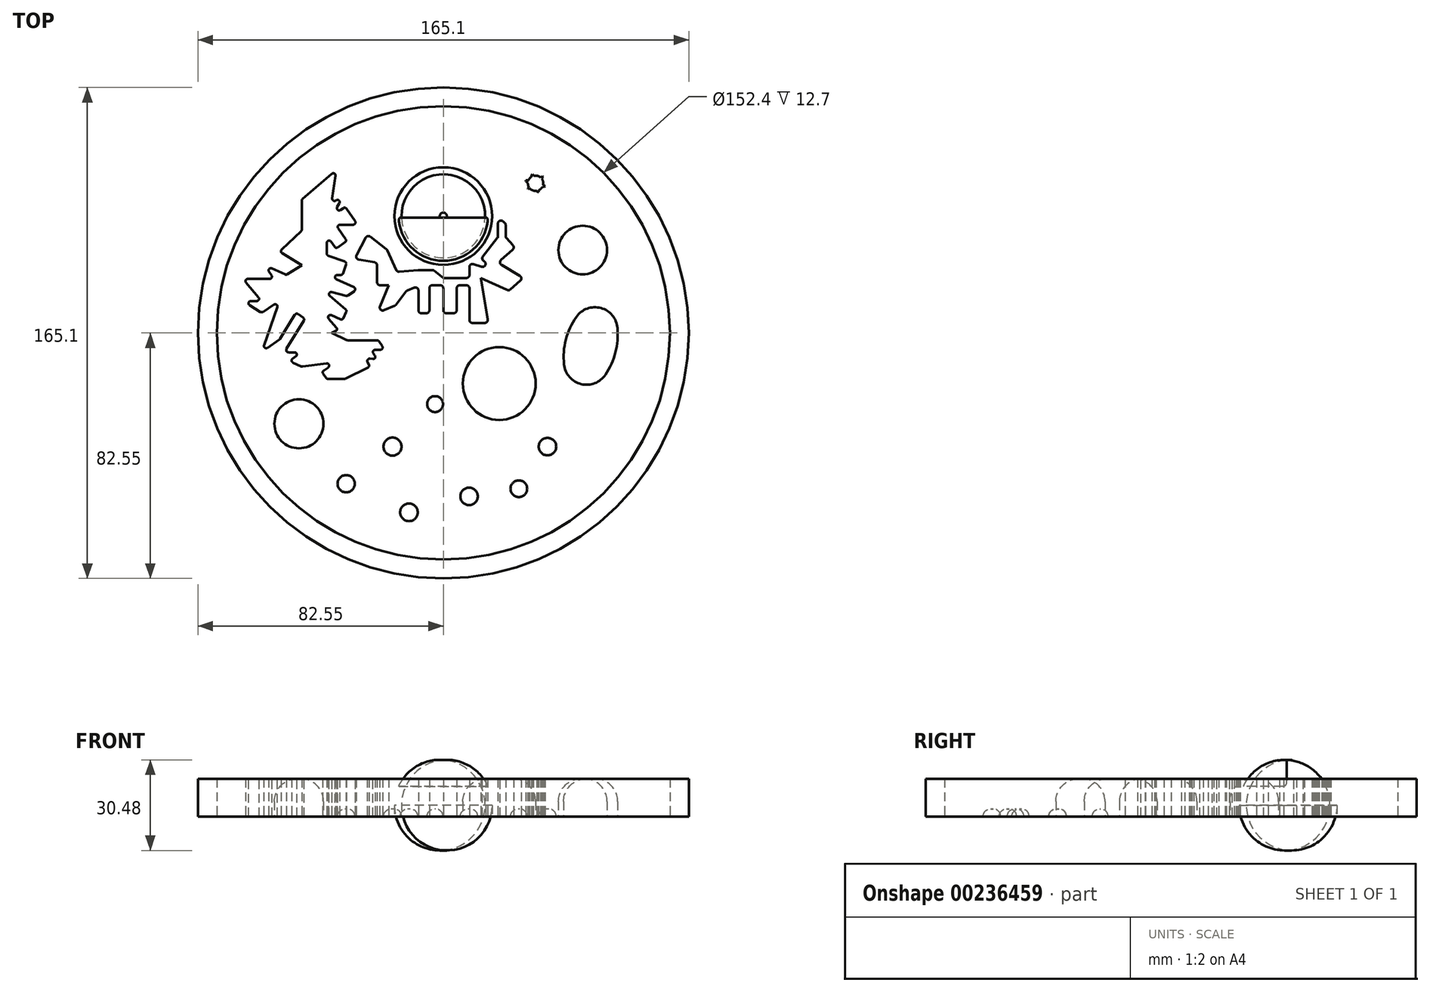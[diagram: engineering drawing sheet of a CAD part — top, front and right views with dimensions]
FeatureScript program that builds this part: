
annotation { "Feature Type Name" : "Feature", "Feature Type Description" : "" }
export const myFeature = defineFeature(function(context is Context, id is Id, definition is map)
    precondition{}
    {
        {
            var Q0;
            Q0=qCreatedBy(makeId("Top.planeOp"),FACE);
            var sketch = newSketch(context, id + "F0", { "sketchPlane" : qUnion([Q0])});
            skCircle(sketch, "E0", {"center": v(0, 0) * mm, "radius": 76.2 * mm});
            skCircle(sketch, "E1", {"center": v(0, 0) * mm, "radius": 82.55 * mm});
            skLineSegment(sketch, "E2", {"start": v(76.2, 0) * mm, "end": v(82.55, 0) * mm});
            skLineSegment(sketch, "E3", {"start": v(-76.2, 0) * mm, "end": v(-82.55, 0) * mm});
            skSolve(sketch);
        }
        {
            var Q0;
            {var subQ0=sQuery(id+"F0.wireOp",EDGE,"E2");Q0=makeQuery(id+"F0.imprint","IMPRINT",FACE,{"disambiguationData":[TD([[makeQuery(id+"F0.imprint","IMPRINT",EDGE,{"derivedFrom":subQ0}),1.0]])]});}
            var Q1;
            {var subQ0=sQuery(id+"F0.wireOp",EDGE,"E2");Q1=makeQuery(id+"F0.imprint","IMPRINT",FACE,{"disambiguationData":[TD([[makeQuery(id+"F0.imprint","IMPRINT",EDGE,{"derivedFrom":subQ0}),-1.0]])]});}
            extrude(context, id + "F1", {"entities" : qUnion([Q0, Q1]), "depth" : 12.7 * mm});
        }
        {
            var Q0;
            Q0=qCreatedBy(makeId("Top.planeOp"),FACE);
            var sketch = newSketch(context, id + "F2", { "sketchPlane" : qUnion([Q0])});
            skCircle(sketch, "E4", {"center": v(0, 39.3) * mm, "radius": 16.42 * mm});
            skSolve(sketch);
        }
        {
            var Q0;
            Q0=makeQuery(id+"F2.imprint","IMPRINT",FACE,{"disambiguationData":[TD([[makeQuery(id+"F2.imprint","IMPRINT",EDGE,{"derivedFrom":sQuery(id+"F2.wireOp",EDGE,"E4")}),1.0]])]});
            extrude(context, id + "F3", {"entities" : qUnion([Q0]), "depth" : 19.05 * mm});
        }
        {
            var Q0;
            Q0=makeQuery(id+"F3.opExtrude","CAP_EDGE",EDGE,{"disambiguationData":[OSD([sQuery(id+"F2.wireOp",EDGE,"E4")])],"isStart":false});
            fillet(context, id + "F4", {"entities" : qUnion([Q0]), "radius" : 15.24 * mm, "tangentPropagation" : true, "allowEdgeOverflow" : false});
        }
        {
            var Q0;
            Q0=qCreatedBy(makeId("Top.planeOp"),FACE);
            var sketch = newSketch(context, id + "F5", { "sketchPlane" : qUnion([Q0])});
            skLineSegment(sketch, "E5", {"start": v(-8.37, 15.82) * mm, "end": v(-8.37, 6.64) * mm});
            skLineSegment(sketch, "E6", {"start": v(-8.37, 6.64) * mm, "end": v(-4.7, 6.64) * mm});
            skLineSegment(sketch, "E7", {"start": v(-4.7, 6.64) * mm, "end": v(-4.7, 16.03) * mm});
            skLineSegment(sketch, "E8", {"start": v(-4.7, 16.03) * mm, "end": v(0, 16.03) * mm});
            skLineSegment(sketch, "E9", {"start": v(0, 16.03) * mm, "end": v(0, 6.64) * mm});
            skLineSegment(sketch, "E10", {"start": v(0, 6.64) * mm, "end": v(4.5, 6.64) * mm});
            skLineSegment(sketch, "E11", {"start": v(4.5, 6.64) * mm, "end": v(4.5, 16.03) * mm});
            skLineSegment(sketch, "E12", {"start": v(4.5, 16.03) * mm, "end": v(8.78, 16.03) * mm});
            skLineSegment(sketch, "E13", {"start": v(8.78, 16.03) * mm, "end": v(8.78, 3.37) * mm});
            skLineSegment(sketch, "E14", {"start": v(8.78, 3.37) * mm, "end": v(15.1, 3.37) * mm});
            skLineSegment(sketch, "E15", {"start": v(15.1, 3.37) * mm, "end": v(12.66, 18.48) * mm});
            skLineSegment(sketch, "E16", {"start": v(12.66, 18.48) * mm, "end": v(22.05, 14.2) * mm});
            skLineSegment(sketch, "E17", {"start": v(22.05, 14.2) * mm, "end": v(26.95, 18.48) * mm});
            skLineSegment(sketch, "E18", {"start": v(26.95, 18.48) * mm, "end": v(18.38, 23.58) * mm});
            skLineSegment(sketch, "E19", {"start": v(18.38, 23.58) * mm, "end": v(24.1, 28.69) * mm});
            skLineSegment(sketch, "E20", {"start": v(24.1, 28.69) * mm, "end": v(20.95, 32.2) * mm});
            skLineSegment(sketch, "E21", {"start": v(20.95, 32.2) * mm, "end": v(20.95, 36.86) * mm});
            skLineSegment(sketch, "E22", {"start": v(20.95, 36.86) * mm, "end": v(18.38, 38.9) * mm});
            skLineSegment(sketch, "E23", {"start": v(18.38, 38.9) * mm, "end": v(18.38, 32.16) * mm});
            skLineSegment(sketch, "E24", {"start": v(18.38, 32.16) * mm, "end": v(15.1, 28.04) * mm});
            skLineSegment(sketch, "E25", {"start": v(15.1, 28.04) * mm, "end": v(12.66, 24.95) * mm});
            skLineSegment(sketch, "E26", {"start": v(18.38, 20.52) * mm, "end": v(12.66, 24.95) * mm});
            skLineSegment(sketch, "E27", {"start": v(18.38, 20.52) * mm, "end": v(8.78, 23.58) * mm});
            skLineSegment(sketch, "E28", {"start": v(8.78, 23.58) * mm, "end": v(8.78, 18.48) * mm});
            skLineSegment(sketch, "E29", {"start": v(8.78, 18.48) * mm, "end": v(0, 18.48) * mm});
            skLineSegment(sketch, "E30", {"start": v(0, 18.48) * mm, "end": v(-3.4, 21.17) * mm});
            skLineSegment(sketch, "E31", {"start": v(-3.4, 21.17) * mm, "end": v(-8.37, 21.17) * mm});
            skLineSegment(sketch, "E32", {"start": v(-8.37, 21.17) * mm, "end": v(-15.52, 20.52) * mm});
            skLineSegment(sketch, "E33", {"start": v(-15.52, 20.52) * mm, "end": v(-18.99, 28.08) * mm});
            skLineSegment(sketch, "E34", {"start": v(-18.99, 28.08) * mm, "end": v(-25.52, 33.13) * mm});
            skLineSegment(sketch, "E35", {"start": v(-25.52, 33.13) * mm, "end": v(-29.81, 24.95) * mm});
            skLineSegment(sketch, "E36", {"start": v(-29.81, 24.95) * mm, "end": v(-22.26, 23.58) * mm});
            skLineSegment(sketch, "E37", {"start": v(-22.26, 23.58) * mm, "end": v(-22.26, 16.03) * mm});
            skLineSegment(sketch, "E38", {"start": v(-22.26, 16.03) * mm, "end": v(-18.38, 16.03) * mm});
            skLineSegment(sketch, "E39", {"start": v(-18.38, 16.03) * mm, "end": v(-22.26, 6.64) * mm});
            skLineSegment(sketch, "E40", {"start": v(-22.26, 6.64) * mm, "end": v(-16.13, 9.3) * mm});
            skLineSegment(sketch, "E41", {"start": v(-16.13, 9.3) * mm, "end": v(-12.34, 14.2) * mm});
            skLineSegment(sketch, "E42", {"start": v(-12.34, 14.2) * mm, "end": v(-8.37, 15.82) * mm});
            skSolve(sketch);
        }
        {
            var Q0;
            Q0 = qSketchRegion(id + "F5", true);
            extrude(context, id + "F6", {"entities" : qUnion([Q0]), "depth" : 12.7 * mm});
        }
        {
            var Q0;
            Q0=makeQuery(id+"F6.opExtrude","SWEPT_EDGE",EDGE,{"disambiguationData":[OSD([sQuery(id+"F5.wireOp",EDGE,"E39"),sQuery(id+"F5.wireOp",EDGE,"E40")])]});
            var Q1;
            Q1=makeQuery(id+"F6.opExtrude","SWEPT_EDGE",EDGE,{"disambiguationData":[OSD([sQuery(id+"F5.wireOp",EDGE,"E40"),sQuery(id+"F5.wireOp",EDGE,"E41")])]});
            var Q2;
            Q2=makeQuery(id+"F6.opExtrude","SWEPT_EDGE",EDGE,{"disambiguationData":[OSD([sQuery(id+"F5.wireOp",EDGE,"E41"),sQuery(id+"F5.wireOp",EDGE,"E42")])]});
            var Q3;
            Q3=makeQuery(id+"F6.opExtrude","SWEPT_EDGE",EDGE,{"disambiguationData":[OSD([sQuery(id+"F5.wireOp",EDGE,"E5"),sQuery(id+"F5.wireOp",EDGE,"E42")])]});
            var Q4;
            Q4=makeQuery(id+"F6.opExtrude","SWEPT_EDGE",EDGE,{"disambiguationData":[OSD([sQuery(id+"F5.wireOp",EDGE,"E37"),sQuery(id+"F5.wireOp",EDGE,"E38")])]});
            var Q5;
            Q5=makeQuery(id+"F6.opExtrude","SWEPT_EDGE",EDGE,{"disambiguationData":[OSD([sQuery(id+"F5.wireOp",EDGE,"E36"),sQuery(id+"F5.wireOp",EDGE,"E37")])]});
            var Q6;
            Q6=makeQuery(id+"F6.opExtrude","SWEPT_EDGE",EDGE,{"disambiguationData":[OSD([sQuery(id+"F5.wireOp",EDGE,"E35"),sQuery(id+"F5.wireOp",EDGE,"E36")])]});
            var Q7;
            Q7=makeQuery(id+"F6.opExtrude","SWEPT_EDGE",EDGE,{"disambiguationData":[OSD([sQuery(id+"F5.wireOp",EDGE,"E8"),sQuery(id+"F5.wireOp",EDGE,"E9")])]});
            var Q8;
            Q8=makeQuery(id+"F6.opExtrude","SWEPT_EDGE",EDGE,{"disambiguationData":[OSD([sQuery(id+"F5.wireOp",EDGE,"E7"),sQuery(id+"F5.wireOp",EDGE,"E8")])]});
            var Q9;
            Q9=makeQuery(id+"F6.opExtrude","SWEPT_EDGE",EDGE,{"disambiguationData":[OSD([sQuery(id+"F5.wireOp",EDGE,"E6"),sQuery(id+"F5.wireOp",EDGE,"E7")])]});
            var Q10;
            Q10=makeQuery(id+"F6.opExtrude","SWEPT_EDGE",EDGE,{"disambiguationData":[OSD([sQuery(id+"F5.wireOp",EDGE,"E5"),sQuery(id+"F5.wireOp",EDGE,"E6")])]});
            var Q11;
            Q11=makeQuery(id+"F6.opExtrude","SWEPT_EDGE",EDGE,{"disambiguationData":[OSD([sQuery(id+"F5.wireOp",EDGE,"E9"),sQuery(id+"F5.wireOp",EDGE,"E10")])]});
            var Q12;
            Q12=makeQuery(id+"F6.opExtrude","SWEPT_EDGE",EDGE,{"disambiguationData":[OSD([sQuery(id+"F5.wireOp",EDGE,"E10"),sQuery(id+"F5.wireOp",EDGE,"E11")])]});
            var Q13;
            Q13=makeQuery(id+"F6.opExtrude","SWEPT_EDGE",EDGE,{"disambiguationData":[OSD([sQuery(id+"F5.wireOp",EDGE,"E11"),sQuery(id+"F5.wireOp",EDGE,"E12")])]});
            var Q14;
            Q14=makeQuery(id+"F6.opExtrude","SWEPT_EDGE",EDGE,{"disambiguationData":[OSD([sQuery(id+"F5.wireOp",EDGE,"E12"),sQuery(id+"F5.wireOp",EDGE,"E13")])]});
            var Q15;
            Q15=makeQuery(id+"F6.opExtrude","SWEPT_EDGE",EDGE,{"disambiguationData":[OSD([sQuery(id+"F5.wireOp",EDGE,"E13"),sQuery(id+"F5.wireOp",EDGE,"E14")])]});
            var Q16;
            Q16=makeQuery(id+"F6.opExtrude","SWEPT_EDGE",EDGE,{"disambiguationData":[OSD([sQuery(id+"F5.wireOp",EDGE,"E14"),sQuery(id+"F5.wireOp",EDGE,"E15")])]});
            var Q17;
            Q17=makeQuery(id+"F6.opExtrude","SWEPT_EDGE",EDGE,{"disambiguationData":[OSD([sQuery(id+"F5.wireOp",EDGE,"E16"),sQuery(id+"F5.wireOp",EDGE,"E17")])]});
            var Q18;
            Q18=makeQuery(id+"F6.opExtrude","SWEPT_EDGE",EDGE,{"disambiguationData":[OSD([sQuery(id+"F5.wireOp",EDGE,"E17"),sQuery(id+"F5.wireOp",EDGE,"E18")])]});
            var Q19;
            Q19=makeQuery(id+"F6.opExtrude","SWEPT_EDGE",EDGE,{"disambiguationData":[OSD([sQuery(id+"F5.wireOp",EDGE,"E18"),sQuery(id+"F5.wireOp",EDGE,"E19")])]});
            var Q20;
            Q20=makeQuery(id+"F6.opExtrude","SWEPT_EDGE",EDGE,{"disambiguationData":[OSD([sQuery(id+"F5.wireOp",EDGE,"E19"),sQuery(id+"F5.wireOp",EDGE,"E20")])]});
            var Q21;
            Q21=makeQuery(id+"F6.opExtrude","SWEPT_EDGE",EDGE,{"disambiguationData":[OSD([sQuery(id+"F5.wireOp",EDGE,"E20"),sQuery(id+"F5.wireOp",EDGE,"E21")])]});
            var Q22;
            Q22=makeQuery(id+"F6.opExtrude","SWEPT_EDGE",EDGE,{"disambiguationData":[OSD([sQuery(id+"F5.wireOp",EDGE,"E21"),sQuery(id+"F5.wireOp",EDGE,"E22")])]});
            var Q23;
            Q23=makeQuery(id+"F6.opExtrude","SWEPT_EDGE",EDGE,{"disambiguationData":[OSD([sQuery(id+"F5.wireOp",EDGE,"E22"),sQuery(id+"F5.wireOp",EDGE,"E23")])]});
            var Q24;
            Q24=makeQuery(id+"F6.opExtrude","SWEPT_EDGE",EDGE,{"disambiguationData":[OSD([sQuery(id+"F5.wireOp",EDGE,"E23"),sQuery(id+"F5.wireOp",EDGE,"E24")])]});
            var Q25;
            Q25=makeQuery(id+"F6.opExtrude","SWEPT_EDGE",EDGE,{"disambiguationData":[OSD([sQuery(id+"F5.wireOp",EDGE,"E25"),sQuery(id+"F5.wireOp",EDGE,"E26")])]});
            var Q26;
            Q26=makeQuery(id+"F6.opExtrude","SWEPT_EDGE",EDGE,{"disambiguationData":[OSD([sQuery(id+"F5.wireOp",EDGE,"E26"),sQuery(id+"F5.wireOp",EDGE,"E27")])]});
            var Q27;
            Q27=makeQuery(id+"F6.opExtrude","SWEPT_EDGE",EDGE,{"disambiguationData":[OSD([sQuery(id+"F5.wireOp",EDGE,"E28"),sQuery(id+"F5.wireOp",EDGE,"E29")])]});
            var Q28;
            Q28=makeQuery(id+"F6.opExtrude","SWEPT_EDGE",EDGE,{"disambiguationData":[OSD([sQuery(id+"F5.wireOp",EDGE,"E27"),sQuery(id+"F5.wireOp",EDGE,"E28")])]});
            var Q29;
            Q29=makeQuery(id+"F6.opExtrude","SWEPT_EDGE",EDGE,{"disambiguationData":[OSD([sQuery(id+"F5.wireOp",EDGE,"E31"),sQuery(id+"F5.wireOp",EDGE,"E32")])]});
            var Q30;
            Q30=makeQuery(id+"F6.opExtrude","SWEPT_EDGE",EDGE,{"disambiguationData":[OSD([sQuery(id+"F5.wireOp",EDGE,"E30"),sQuery(id+"F5.wireOp",EDGE,"E31")])]});
            var Q31;
            Q31=makeQuery(id+"F6.opExtrude","SWEPT_EDGE",EDGE,{"disambiguationData":[OSD([sQuery(id+"F5.wireOp",EDGE,"E33"),sQuery(id+"F5.wireOp",EDGE,"E34")])]});
            var Q32;
            Q32=makeQuery(id+"F6.opExtrude","SWEPT_EDGE",EDGE,{"disambiguationData":[OSD([sQuery(id+"F5.wireOp",EDGE,"E32"),sQuery(id+"F5.wireOp",EDGE,"E33")])]});
            var Q33;
            Q33=makeQuery(id+"F6.opExtrude","SWEPT_EDGE",EDGE,{"disambiguationData":[OSD([sQuery(id+"F5.wireOp",EDGE,"E34"),sQuery(id+"F5.wireOp",EDGE,"E35")])]});
            fillet(context, id + "F7", {"entities" : qUnion([Q0, Q1, Q2, Q3, Q4, Q5, Q6, Q7, Q8, Q9, Q10, Q11, Q12, Q13, Q14, Q15, Q16, Q17, Q18, Q19, Q20, Q21, Q22, Q23, Q24, Q25, Q26, Q27, Q28, Q29, Q30, Q31, Q32, Q33]), "radius" : 1.02 * mm, "tangentPropagation" : true, "allowEdgeOverflow" : false});
        }
        {
            var Q0;
            Q0=makeQuery(id+"F3.opExtrude","CAP_FACE",FACE,{"disambiguationData":[OSD([sQuery(id+"F2.wireOp",EDGE,"E4")])],"isStart":false});
            var sketch = newSketch(context, id + "F8", { "sketchPlane" : qUnion([Q0])});
            skLineSegment(sketch, "E43.bottom", {"start": v(16.4, 38.82) * mm, "end": v(-16.5, 38.82) * mm});
            skArc(sketch, "E44", {"start": v(-16.5, 38.82) * mm, "mid": v(-0.05, 22.9) * mm, "end": v(16.4, 38.82) * mm});
            skSolve(sketch);
        }
        {
            var Q0;
            {var subQ0=sQuery(id+"F8.wireOp",EDGE,"E44");Q0=makeQuery(id+"F8.imprint","IMPRINT",FACE,{"disambiguationData":[TD([[makeQuery(id+"F8.imprint","IMPRINT",EDGE,{"derivedFrom":subQ0}),1.0]])]});}
            extrude(context, id + "F9", {"entities" : qUnion([Q0]), "operationType" : NewBodyOperationType.REMOVE, "oppositeDirection" : true, "depth" : 8.9 * mm});
        }
        {
            var Q0;
            Q0=makeQuery(id+"F3.opExtrude","CAP_FACE",FACE,{"disambiguationData":[OSD([sQuery(id+"F2.wireOp",EDGE,"E4")])],"isStart":false});
            var sketch = newSketch(context, id + "F10", { "sketchPlane" : qUnion([Q0])});
            skLineSegment(sketch, "E45", {"start": v(-1.08, 38.82) * mm, "end": v(1.08, 38.82) * mm});
            skArc(sketch, "E46", {"start": v(-1.08, 38.82) * mm, "mid": v(0, 38.13) * mm, "end": v(1.08, 38.82) * mm});
            skSolve(sketch);
        }
        {
            var Q0;
            Q0=makeQuery(id+"F10.imprint","IMPRINT",FACE,{"disambiguationData":[TD([[makeQuery(id+"F10.imprint","IMPRINT",EDGE,{"derivedFrom":sQuery(id+"F10.wireOp",EDGE,"E45")}),-1.0]])]});
            extrude(context, id + "F11", {"entities" : qUnion([Q0]), "operationType" : NewBodyOperationType.REMOVE, "oppositeDirection" : true, "depth" : 8.9 * mm});
        }
        {
            var Q0;
            {var subQ0=sQuery(id+"F8.wireOp",EDGE,"E44");var subQ1=sQuery(id+"F8.wireOp",EDGE,"E43.bottom");Q0=makeQuery(id+"F11.boolean.opBoolean","MERGE",EDGE,{"derivedFrom":[makeQuery(id+"F9.boolean.opBoolean","COPY",EDGE,{"derivedFrom":makeQuery(id+"F9.opExtrude","CAP_EDGE",EDGE,{"disambiguationData":[OSD([subQ1]),TDD([makeQuery(id+"F8.imprint","IMPRINT",EDGE,{"disambiguationData":[TD([[makeQuery(id+"F8.imprint","INTERSECT",VERTEX,{"disambiguationData":[OD(0.0)],"derivedFrom":[subQ1,subQ0]}),-1.0]])],"derivedFrom":subQ1})])],"isStart":false})}),makeQuery(id+"F9.boolean.opBoolean","COPY",EDGE,{"derivedFrom":makeQuery(id+"F9.opExtrude","CAP_EDGE",EDGE,{"disambiguationData":[OSD([subQ1]),TDD([makeQuery(id+"F8.imprint","IMPRINT",EDGE,{"disambiguationData":[TD([[makeQuery(id+"F8.imprint","INTERSECT",VERTEX,{"disambiguationData":[OD(1.0)],"derivedFrom":[subQ1,subQ0]}),1.0]])],"derivedFrom":subQ1})])],"isStart":false})}),makeQuery(id+"F11.opExtrude","CAP_EDGE",EDGE,{"disambiguationData":[OSD([sQuery(id+"F10.wireOp",EDGE,"E45")])],"isStart":false})]});}
            fillet(context, id + "F12", {"entities" : qUnion([Q0]), "radius" : 1.27 * mm, "tangentPropagation" : true, "allowEdgeOverflow" : false});
        }
        {
            var Q0;
            Q0=qCreatedBy(makeId("Top.planeOp"),FACE);
            var sketch = newSketch(context, id + "F13", { "sketchPlane" : qUnion([Q0])});
            skArc(sketch, "E47", {"start": v(45.24, -22.29) * mm, "mid": v(57.87, -6.54) * mm, "end": v(54.48, 13.37) * mm});
            skArc(sketch, "E48", {"start": v(54.48, 13.37) * mm, "mid": v(41.22, -2.22) * mm, "end": v(45.24, -22.29) * mm});
            skSolve(sketch);
        }
        {
            var Q0;
            Q0=makeQuery(id+"F13.imprint","IMPRINT",FACE,{"disambiguationData":[TD([[makeQuery(id+"F13.imprint","IMPRINT",EDGE,{"derivedFrom":sQuery(id+"F13.wireOp",EDGE,"E47")}),1.0]])]});
            extrude(context, id + "F14", {"entities" : qUnion([Q0]), "depth" : 12.7 * mm});
        }
        {
            var Q0;
            {var subQ0=sQuery(id+"F13.wireOp",EDGE,"E48");var subQ1=sQuery(id+"F13.wireOp",EDGE,"E47");Q0=makeQuery(id+"F14.opExtrude","SWEPT_EDGE",EDGE,{"disambiguationData":[OSD([subQ1,subQ0]),TDD([makeQuery(id+"F13.imprint","INTERSECT",VERTEX,{"disambiguationData":[OD(0.0)],"derivedFrom":[subQ1,subQ0]})])]});}
            var Q1;
            {var subQ0=sQuery(id+"F13.wireOp",EDGE,"E48");var subQ1=sQuery(id+"F13.wireOp",EDGE,"E47");Q1=makeQuery(id+"F14.opExtrude","SWEPT_EDGE",EDGE,{"disambiguationData":[OSD([subQ1,subQ0]),TDD([makeQuery(id+"F13.imprint","INTERSECT",VERTEX,{"disambiguationData":[OD(1.0)],"derivedFrom":[subQ1,subQ0]})])]});}
            var Q2;
            Q2=makeQuery(id+"F14.opExtrude","CAP_EDGE",EDGE,{"disambiguationData":[OSD([sQuery(id+"F13.wireOp",EDGE,"E47")])],"isStart":false});
            var Q3;
            Q3=makeQuery(id+"F14.opExtrude","CAP_EDGE",EDGE,{"disambiguationData":[OSD([sQuery(id+"F13.wireOp",EDGE,"E48")])],"isStart":false});
            fillet(context, id + "F15", {"entities" : qUnion([Q0, Q1, Q2, Q3]), "radius" : 7.62 * mm, "tangentPropagation" : true, "allowEdgeOverflow" : false});
        }
        {
            var Q0;
            Q0=qCreatedBy(makeId("Top.planeOp"),FACE);
            var sketch = newSketch(context, id + "F16", { "sketchPlane" : qUnion([Q0])});
            skLineSegment(sketch, "E49", {"start": v(-35.93, 54.84) * mm, "end": v(-47.58, 44.86) * mm});
            skLineSegment(sketch, "E50", {"start": v(-47.58, 44.86) * mm, "end": v(-47.58, 34.46) * mm});
            skLineSegment(sketch, "E51", {"start": v(-47.58, 34.46) * mm, "end": v(-55.07, 27.39) * mm});
            skLineSegment(sketch, "E52", {"start": v(-33.02, -15.46) * mm, "end": v(-24.7, -11.3) * mm});
            skLineSegment(sketch, "E53", {"start": v(-24.7, -11.3) * mm, "end": v(-26.12, -8.47) * mm});
            skLineSegment(sketch, "E54", {"start": v(-28.86, 36.4) * mm, "end": v(-33.02, 42.44) * mm});
            skLineSegment(sketch, "E55", {"start": v(-33.02, 42.44) * mm, "end": v(-37.6, 39.28) * mm});
            skLineSegment(sketch, "E56", {"start": v(-37.6, 39.28) * mm, "end": v(-33.02, 46.68) * mm});
            skLineSegment(sketch, "E57", {"start": v(-33.02, 46.68) * mm, "end": v(-37.6, 43.53) * mm});
            skLineSegment(sketch, "E58", {"start": v(-37.6, 43.53) * mm, "end": v(-35.93, 54.84) * mm});
            skLineSegment(sketch, "E59", {"start": v(-55.07, 27.39) * mm, "end": v(-47.58, 22.76) * mm});
            skLineSegment(sketch, "E60", {"start": v(-67.43, 10.75) * mm, "end": v(-61.07, 6.81) * mm});
            skLineSegment(sketch, "E61", {"start": v(-61.07, 6.81) * mm, "end": v(-55.07, 10.75) * mm});
            skLineSegment(sketch, "E62", {"start": v(-55.07, 10.75) * mm, "end": v(-61.07, -6.31) * mm});
            skLineSegment(sketch, "E63", {"start": v(-61.07, -6.31) * mm, "end": v(-55.07, -2.18) * mm});
            skLineSegment(sketch, "E64", {"start": v(-55.07, -2.18) * mm, "end": v(-49.51, 6.81) * mm});
            skLineSegment(sketch, "E65", {"start": v(-28.86, 36.4) * mm, "end": v(-36.2, 36.4) * mm});
            skLineSegment(sketch, "E66", {"start": v(-36.2, 36.4) * mm, "end": v(-32.42, 30.92) * mm});
            skLineSegment(sketch, "E67", {"start": v(-32.42, 30.92) * mm, "end": v(-36.14, 28.36) * mm});
            skLineSegment(sketch, "E68", {"start": v(-36.14, 28.36) * mm, "end": v(-39.17, 32.76) * mm});
            skLineSegment(sketch, "E69", {"start": v(-39.17, 32.76) * mm, "end": v(-39.17, 26.14) * mm});
            skLineSegment(sketch, "E70", {"start": v(-39.17, 26.14) * mm, "end": v(-32.42, 23.73) * mm});
            skLineSegment(sketch, "E71", {"start": v(-32.42, 23.73) * mm, "end": v(-33.93, 19.51) * mm});
            skLineSegment(sketch, "E72", {"start": v(-33.93, 19.51) * mm, "end": v(-39.17, 19.51) * mm});
            skLineSegment(sketch, "E73", {"start": v(-39.17, 19.51) * mm, "end": v(-28.86, 14.83) * mm});
            skLineSegment(sketch, "E74", {"start": v(-28.86, 14.83) * mm, "end": v(-32.42, 12.38) * mm});
            skLineSegment(sketch, "E75", {"start": v(-32.42, 12.38) * mm, "end": v(-40.84, 14.65) * mm});
            skLineSegment(sketch, "E76", {"start": v(-40.84, 14.65) * mm, "end": v(-32.42, 7.6) * mm});
            skLineSegment(sketch, "E77", {"start": v(-32.42, 7.6) * mm, "end": v(-33.93, 4.29) * mm});
            skLineSegment(sketch, "E78", {"start": v(-33.93, 4.29) * mm, "end": v(-40.84, 7.43) * mm});
            skLineSegment(sketch, "E79", {"start": v(-32.42, -2.44) * mm, "end": v(-21.93, -2.44) * mm});
            skLineSegment(sketch, "E80", {"start": v(-21.93, -2.44) * mm, "end": v(-19.72, -5.65) * mm});
            skLineSegment(sketch, "E81", {"start": v(-19.72, -5.65) * mm, "end": v(-24.34, -5.65) * mm});
            skLineSegment(sketch, "E82", {"start": v(-33.02, -15.46) * mm, "end": v(-39.17, -15.46) * mm});
            skLineSegment(sketch, "E83", {"start": v(-39.17, -15.46) * mm, "end": v(-40.84, -13.04) * mm});
            skLineSegment(sketch, "E84", {"start": v(-40.84, -13.04) * mm, "end": v(-36.14, -9.8) * mm});
            skLineSegment(sketch, "E85", {"start": v(-36.14, -9.8) * mm, "end": v(-47.58, -11.3) * mm});
            skLineSegment(sketch, "E86", {"start": v(-47.58, -11.3) * mm, "end": v(-51.78, -9.4) * mm});
            skLineSegment(sketch, "E87", {"start": v(-51.78, -9.4) * mm, "end": v(-47.58, -6.5) * mm});
            skLineSegment(sketch, "E88", {"start": v(-47.58, -6.5) * mm, "end": v(-53.44, -6.5) * mm});
            skLineSegment(sketch, "E89", {"start": v(-53.44, -6.5) * mm, "end": v(-46.54, 4.64) * mm});
            skLineSegment(sketch, "E90", {"start": v(-46.54, 4.64) * mm, "end": v(-49.51, 6.81) * mm});
            skLineSegment(sketch, "E91", {"start": v(-67.43, 10.75) * mm, "end": v(-61.07, 10.75) * mm});
            skLineSegment(sketch, "E92", {"start": v(-61.07, 10.75) * mm, "end": v(-67.43, 18.17) * mm});
            skLineSegment(sketch, "E93", {"start": v(-67.43, 18.17) * mm, "end": v(-56.96, 18.17) * mm});
            skLineSegment(sketch, "E94", {"start": v(-56.96, 18.17) * mm, "end": v(-60.2, 22.87) * mm});
            skLineSegment(sketch, "E95", {"start": v(-60.2, 22.87) * mm, "end": v(-52.81, 19.51) * mm});
            skLineSegment(sketch, "E96", {"start": v(-52.81, 19.51) * mm, "end": v(-47.58, 22.76) * mm});
            skLineSegment(sketch, "E97", {"start": v(-32.42, -2.44) * mm, "end": v(-37.52, 0) * mm});
            skLineSegment(sketch, "E98", {"start": v(-37.52, 0) * mm, "end": v(-35.3, 1.04) * mm});
            skLineSegment(sketch, "E99", {"start": v(-35.3, 1.04) * mm, "end": v(-40.84, 7.43) * mm});
            skLineSegment(sketch, "E100", {"start": v(-24.34, -5.65) * mm, "end": v(-22.03, -9) * mm});
            skPoint(sketch, "E100.endSnap0", {"position": v(-22.03, -5.65) * mm});
            skLineSegment(sketch, "E101", {"start": v(-22.03, -9) * mm, "end": v(-26.12, -8.47) * mm});
            skSolve(sketch);
        }
        {
            var Q0;
            Q0=makeQuery(id+"F16.imprint","IMPRINT",FACE,{"disambiguationData":[TD([[makeQuery(id+"F16.imprint","IMPRINT",EDGE,{"derivedFrom":sQuery(id+"F16.wireOp",EDGE,"E49")}),1.0]])]});
            extrude(context, id + "F17", {"entities" : qUnion([Q0]), "depth" : 12.7 * mm});
        }
        {
            var Q0;
            Q0=makeQuery(id+"F17.opExtrude","SWEPT_EDGE",EDGE,{"disambiguationData":[OSD([sQuery(id+"F16.wireOp",EDGE,"E62"),sQuery(id+"F16.wireOp",EDGE,"E63")])]});
            var Q1;
            Q1=makeQuery(id+"F17.opExtrude","SWEPT_EDGE",EDGE,{"disambiguationData":[OSD([sQuery(id+"F16.wireOp",EDGE,"E63"),sQuery(id+"F16.wireOp",EDGE,"E64")])]});
            var Q2;
            Q2=makeQuery(id+"F17.opExtrude","SWEPT_EDGE",EDGE,{"disambiguationData":[OSD([sQuery(id+"F16.wireOp",EDGE,"E64"),sQuery(id+"F16.wireOp",EDGE,"E90")])]});
            var Q3;
            Q3=makeQuery(id+"F17.opExtrude","SWEPT_EDGE",EDGE,{"disambiguationData":[OSD([sQuery(id+"F16.wireOp",EDGE,"E88"),sQuery(id+"F16.wireOp",EDGE,"E89")])]});
            var Q4;
            Q4=makeQuery(id+"F17.opExtrude","SWEPT_EDGE",EDGE,{"disambiguationData":[OSD([sQuery(id+"F16.wireOp",EDGE,"E86"),sQuery(id+"F16.wireOp",EDGE,"E87")])]});
            var Q5;
            Q5=makeQuery(id+"F17.opExtrude","SWEPT_EDGE",EDGE,{"disambiguationData":[OSD([sQuery(id+"F16.wireOp",EDGE,"E87"),sQuery(id+"F16.wireOp",EDGE,"E88")])]});
            var Q6;
            Q6=makeQuery(id+"F17.opExtrude","SWEPT_EDGE",EDGE,{"disambiguationData":[OSD([sQuery(id+"F16.wireOp",EDGE,"E85"),sQuery(id+"F16.wireOp",EDGE,"E86")])]});
            var Q7;
            Q7=makeQuery(id+"F17.opExtrude","SWEPT_EDGE",EDGE,{"disambiguationData":[OSD([sQuery(id+"F16.wireOp",EDGE,"E84"),sQuery(id+"F16.wireOp",EDGE,"E85")])]});
            var Q8;
            Q8=makeQuery(id+"F17.opExtrude","SWEPT_EDGE",EDGE,{"disambiguationData":[OSD([sQuery(id+"F16.wireOp",EDGE,"E82"),sQuery(id+"F16.wireOp",EDGE,"E83")])]});
            var Q9;
            Q9=makeQuery(id+"F17.opExtrude","SWEPT_EDGE",EDGE,{"disambiguationData":[OSD([sQuery(id+"F16.wireOp",EDGE,"E83"),sQuery(id+"F16.wireOp",EDGE,"E84")])]});
            var Q10;
            Q10=makeQuery(id+"F17.opExtrude","SWEPT_EDGE",EDGE,{"disambiguationData":[OSD([sQuery(id+"F16.wireOp",EDGE,"E52"),sQuery(id+"F16.wireOp",EDGE,"E82")])]});
            var Q11;
            Q11=makeQuery(id+"F17.opExtrude","SWEPT_EDGE",EDGE,{"disambiguationData":[OSD([sQuery(id+"F16.wireOp",EDGE,"E52"),sQuery(id+"F16.wireOp",EDGE,"E53")])]});
            var Q12;
            Q12=makeQuery(id+"F17.opExtrude","SWEPT_EDGE",EDGE,{"disambiguationData":[OSD([sQuery(id+"F16.wireOp",EDGE,"E53"),sQuery(id+"F16.wireOp",EDGE,"E101")])]});
            var Q13;
            Q13=makeQuery(id+"F17.opExtrude","SWEPT_EDGE",EDGE,{"disambiguationData":[OSD([sQuery(id+"F16.wireOp",EDGE,"E100"),sQuery(id+"F16.wireOp",EDGE,"E101")])]});
            var Q14;
            Q14=makeQuery(id+"F17.opExtrude","SWEPT_EDGE",EDGE,{"disambiguationData":[OSD([sQuery(id+"F16.wireOp",EDGE,"E81"),sQuery(id+"F16.wireOp",EDGE,"E100")])]});
            var Q15;
            Q15=makeQuery(id+"F17.opExtrude","SWEPT_EDGE",EDGE,{"disambiguationData":[OSD([sQuery(id+"F16.wireOp",EDGE,"E80"),sQuery(id+"F16.wireOp",EDGE,"E81")])]});
            var Q16;
            Q16=makeQuery(id+"F17.opExtrude","SWEPT_EDGE",EDGE,{"disambiguationData":[OSD([sQuery(id+"F16.wireOp",EDGE,"E79"),sQuery(id+"F16.wireOp",EDGE,"E80")])]});
            var Q17;
            Q17=makeQuery(id+"F17.opExtrude","SWEPT_EDGE",EDGE,{"disambiguationData":[OSD([sQuery(id+"F16.wireOp",EDGE,"E79"),sQuery(id+"F16.wireOp",EDGE,"E97")])]});
            var Q18;
            Q18=makeQuery(id+"F17.opExtrude","SWEPT_EDGE",EDGE,{"disambiguationData":[OSD([sQuery(id+"F16.wireOp",EDGE,"E98"),sQuery(id+"F16.wireOp",EDGE,"E99")])]});
            var Q19;
            Q19=makeQuery(id+"F17.opExtrude","SWEPT_EDGE",EDGE,{"disambiguationData":[OSD([sQuery(id+"F16.wireOp",EDGE,"E78"),sQuery(id+"F16.wireOp",EDGE,"E99")])]});
            var Q20;
            Q20=makeQuery(id+"F17.opExtrude","SWEPT_EDGE",EDGE,{"disambiguationData":[OSD([sQuery(id+"F16.wireOp",EDGE,"E77"),sQuery(id+"F16.wireOp",EDGE,"E78")])]});
            var Q21;
            Q21=makeQuery(id+"F17.opExtrude","SWEPT_EDGE",EDGE,{"disambiguationData":[OSD([sQuery(id+"F16.wireOp",EDGE,"E75"),sQuery(id+"F16.wireOp",EDGE,"E76")])]});
            var Q22;
            Q22=makeQuery(id+"F17.opExtrude","SWEPT_EDGE",EDGE,{"disambiguationData":[OSD([sQuery(id+"F16.wireOp",EDGE,"E76"),sQuery(id+"F16.wireOp",EDGE,"E77")])]});
            var Q23;
            Q23=makeQuery(id+"F17.opExtrude","SWEPT_EDGE",EDGE,{"disambiguationData":[OSD([sQuery(id+"F16.wireOp",EDGE,"E74"),sQuery(id+"F16.wireOp",EDGE,"E75")])]});
            var Q24;
            Q24=makeQuery(id+"F17.opExtrude","SWEPT_EDGE",EDGE,{"disambiguationData":[OSD([sQuery(id+"F16.wireOp",EDGE,"E73"),sQuery(id+"F16.wireOp",EDGE,"E74")])]});
            var Q25;
            Q25=makeQuery(id+"F17.opExtrude","SWEPT_EDGE",EDGE,{"disambiguationData":[OSD([sQuery(id+"F16.wireOp",EDGE,"E72"),sQuery(id+"F16.wireOp",EDGE,"E73")])]});
            var Q26;
            Q26=makeQuery(id+"F17.opExtrude","SWEPT_EDGE",EDGE,{"disambiguationData":[OSD([sQuery(id+"F16.wireOp",EDGE,"E71"),sQuery(id+"F16.wireOp",EDGE,"E72")])]});
            var Q27;
            Q27=makeQuery(id+"F17.opExtrude","SWEPT_EDGE",EDGE,{"disambiguationData":[OSD([sQuery(id+"F16.wireOp",EDGE,"E70"),sQuery(id+"F16.wireOp",EDGE,"E71")])]});
            var Q28;
            Q28=makeQuery(id+"F17.opExtrude","SWEPT_EDGE",EDGE,{"disambiguationData":[OSD([sQuery(id+"F16.wireOp",EDGE,"E69"),sQuery(id+"F16.wireOp",EDGE,"E70")])]});
            var Q29;
            Q29=makeQuery(id+"F17.opExtrude","SWEPT_EDGE",EDGE,{"disambiguationData":[OSD([sQuery(id+"F16.wireOp",EDGE,"E68"),sQuery(id+"F16.wireOp",EDGE,"E69")])]});
            var Q30;
            Q30=makeQuery(id+"F17.opExtrude","SWEPT_EDGE",EDGE,{"disambiguationData":[OSD([sQuery(id+"F16.wireOp",EDGE,"E66"),sQuery(id+"F16.wireOp",EDGE,"E67")])]});
            var Q31;
            Q31=makeQuery(id+"F17.opExtrude","SWEPT_EDGE",EDGE,{"disambiguationData":[OSD([sQuery(id+"F16.wireOp",EDGE,"E67"),sQuery(id+"F16.wireOp",EDGE,"E68")])]});
            var Q32;
            Q32=makeQuery(id+"F17.opExtrude","SWEPT_EDGE",EDGE,{"disambiguationData":[OSD([sQuery(id+"F16.wireOp",EDGE,"E65"),sQuery(id+"F16.wireOp",EDGE,"E66")])]});
            var Q33;
            Q33=makeQuery(id+"F17.opExtrude","SWEPT_EDGE",EDGE,{"disambiguationData":[OSD([sQuery(id+"F16.wireOp",EDGE,"E54"),sQuery(id+"F16.wireOp",EDGE,"E65")])]});
            var Q34;
            Q34=makeQuery(id+"F17.opExtrude","SWEPT_EDGE",EDGE,{"disambiguationData":[OSD([sQuery(id+"F16.wireOp",EDGE,"E55"),sQuery(id+"F16.wireOp",EDGE,"E56")])]});
            var Q35;
            Q35=makeQuery(id+"F17.opExtrude","SWEPT_EDGE",EDGE,{"disambiguationData":[OSD([sQuery(id+"F16.wireOp",EDGE,"E54"),sQuery(id+"F16.wireOp",EDGE,"E55")])]});
            var Q36;
            Q36=makeQuery(id+"F17.opExtrude","SWEPT_EDGE",EDGE,{"disambiguationData":[OSD([sQuery(id+"F16.wireOp",EDGE,"E56"),sQuery(id+"F16.wireOp",EDGE,"E57")])]});
            var Q37;
            Q37=makeQuery(id+"F17.opExtrude","SWEPT_EDGE",EDGE,{"disambiguationData":[OSD([sQuery(id+"F16.wireOp",EDGE,"E57"),sQuery(id+"F16.wireOp",EDGE,"E58")])]});
            var Q38;
            Q38=makeQuery(id+"F17.opExtrude","SWEPT_EDGE",EDGE,{"disambiguationData":[OSD([sQuery(id+"F16.wireOp",EDGE,"E49"),sQuery(id+"F16.wireOp",EDGE,"E58")])]});
            var Q39;
            Q39=makeQuery(id+"F17.opExtrude","SWEPT_EDGE",EDGE,{"disambiguationData":[OSD([sQuery(id+"F16.wireOp",EDGE,"E50"),sQuery(id+"F16.wireOp",EDGE,"E51")])]});
            var Q40;
            Q40=makeQuery(id+"F17.opExtrude","SWEPT_EDGE",EDGE,{"disambiguationData":[OSD([sQuery(id+"F16.wireOp",EDGE,"E49"),sQuery(id+"F16.wireOp",EDGE,"E50")])]});
            var Q41;
            Q41=makeQuery(id+"F17.opExtrude","SWEPT_EDGE",EDGE,{"disambiguationData":[OSD([sQuery(id+"F16.wireOp",EDGE,"E51"),sQuery(id+"F16.wireOp",EDGE,"E59")])]});
            var Q42;
            Q42=makeQuery(id+"F17.opExtrude","SWEPT_EDGE",EDGE,{"disambiguationData":[OSD([sQuery(id+"F16.wireOp",EDGE,"E95"),sQuery(id+"F16.wireOp",EDGE,"E96")])]});
            var Q43;
            Q43=makeQuery(id+"F17.opExtrude","SWEPT_EDGE",EDGE,{"disambiguationData":[OSD([sQuery(id+"F16.wireOp",EDGE,"E94"),sQuery(id+"F16.wireOp",EDGE,"E95")])]});
            var Q44;
            Q44=makeQuery(id+"F17.opExtrude","SWEPT_EDGE",EDGE,{"disambiguationData":[OSD([sQuery(id+"F16.wireOp",EDGE,"E93"),sQuery(id+"F16.wireOp",EDGE,"E94")])]});
            var Q45;
            Q45=makeQuery(id+"F17.opExtrude","SWEPT_EDGE",EDGE,{"disambiguationData":[OSD([sQuery(id+"F16.wireOp",EDGE,"E92"),sQuery(id+"F16.wireOp",EDGE,"E93")])]});
            var Q46;
            Q46=makeQuery(id+"F17.opExtrude","SWEPT_EDGE",EDGE,{"disambiguationData":[OSD([sQuery(id+"F16.wireOp",EDGE,"E91"),sQuery(id+"F16.wireOp",EDGE,"E92")])]});
            var Q47;
            Q47=makeQuery(id+"F17.opExtrude","SWEPT_EDGE",EDGE,{"disambiguationData":[OSD([sQuery(id+"F16.wireOp",EDGE,"E60"),sQuery(id+"F16.wireOp",EDGE,"E91")])]});
            var Q48;
            Q48=makeQuery(id+"F17.opExtrude","SWEPT_EDGE",EDGE,{"disambiguationData":[OSD([sQuery(id+"F16.wireOp",EDGE,"E61"),sQuery(id+"F16.wireOp",EDGE,"E62")])]});
            var Q49;
            Q49=makeQuery(id+"F17.opExtrude","SWEPT_EDGE",EDGE,{"disambiguationData":[OSD([sQuery(id+"F16.wireOp",EDGE,"E60"),sQuery(id+"F16.wireOp",EDGE,"E61")])]});
            var Q50;
            Q50=makeQuery(id+"F17.opExtrude","SWEPT_EDGE",EDGE,{"disambiguationData":[OSD([sQuery(id+"F16.wireOp",EDGE,"E89"),sQuery(id+"F16.wireOp",EDGE,"E90")])]});
            fillet(context, id + "F18", {"entities" : qUnion([Q0, Q1, Q2, Q3, Q4, Q5, Q6, Q7, Q8, Q9, Q10, Q11, Q12, Q13, Q14, Q15, Q16, Q17, Q18, Q19, Q20, Q21, Q22, Q23, Q24, Q25, Q26, Q27, Q28, Q29, Q30, Q31, Q32, Q33, Q34, Q35, Q36, Q37, Q38, Q39, Q40, Q41, Q42, Q43, Q44, Q45, Q46, Q47, Q48, Q49, Q50]), "radius" : 0.76 * mm, "tangentPropagation" : true, "allowEdgeOverflow" : false});
        }
        {
            var Q0;
            Q0=qCreatedBy(makeId("Top.planeOp"),FACE);
            var sketch = newSketch(context, id + "F19", { "sketchPlane" : qUnion([Q0])});
            skCircle(sketch, "E102", {"center": v(35.04, -38.22) * mm, "radius": 2.94 * mm});
            skCircle(sketch, "E103", {"center": v(-11.55, -60.32) * mm, "radius": 2.96 * mm});
            skCircle(sketch, "E104", {"center": v(8.66, -54.94) * mm, "radius": 2.94 * mm});
            skCircle(sketch, "E105", {"center": v(25.4, -52.37) * mm, "radius": 2.8 * mm});
            skCircle(sketch, "E106", {"center": v(-2.78, -23.91) * mm, "radius": 2.67 * mm});
            skCircle(sketch, "E107", {"center": v(-17.08, -38.22) * mm, "radius": 3.03 * mm});
            skCircle(sketch, "E108", {"center": v(-32.66, -50.7) * mm, "radius": 2.91 * mm});
            skSolve(sketch);
        }
        {
            var Q0;
            Q0=makeQuery(id+"F19.imprint","IMPRINT",FACE,{"disambiguationData":[TD([[makeQuery(id+"F19.imprint","IMPRINT",EDGE,{"derivedFrom":sQuery(id+"F19.wireOp",EDGE,"E108")}),1.0]])]});
            var Q1;
            Q1=makeQuery(id+"F19.imprint","IMPRINT",FACE,{"disambiguationData":[TD([[makeQuery(id+"F19.imprint","IMPRINT",EDGE,{"derivedFrom":sQuery(id+"F19.wireOp",EDGE,"Hh2HkUg6-tROa-9LwI-MVmK-pOOwmGKrsJ4V")}),1.0]])]});
            var Q2;
            Q2=makeQuery(id+"F19.imprint","IMPRINT",FACE,{"disambiguationData":[TD([[makeQuery(id+"F19.imprint","IMPRINT",EDGE,{"derivedFrom":sQuery(id+"F19.wireOp",EDGE,"E107")}),1.0]])]});
            var Q3;
            Q3=makeQuery(id+"F19.imprint","IMPRINT",FACE,{"disambiguationData":[TD([[makeQuery(id+"F19.imprint","IMPRINT",EDGE,{"derivedFrom":sQuery(id+"F19.wireOp",EDGE,"E106")}),1.0]])]});
            var Q4;
            Q4=makeQuery(id+"F19.imprint","IMPRINT",FACE,{"disambiguationData":[TD([[makeQuery(id+"F19.imprint","IMPRINT",EDGE,{"derivedFrom":sQuery(id+"F19.wireOp",EDGE,"E103")}),1.0]])]});
            var Q5;
            Q5=makeQuery(id+"F19.imprint","IMPRINT",FACE,{"disambiguationData":[TD([[makeQuery(id+"F19.imprint","IMPRINT",EDGE,{"derivedFrom":sQuery(id+"F19.wireOp",EDGE,"E104")}),1.0]])]});
            var Q6;
            Q6=makeQuery(id+"F19.imprint","IMPRINT",FACE,{"disambiguationData":[TD([[makeQuery(id+"F19.imprint","IMPRINT",EDGE,{"derivedFrom":sQuery(id+"F19.wireOp",EDGE,"E105")}),1.0]])]});
            var Q7;
            Q7=makeQuery(id+"F19.imprint","IMPRINT",FACE,{"disambiguationData":[TD([[makeQuery(id+"F19.imprint","IMPRINT",EDGE,{"derivedFrom":sQuery(id+"F19.wireOp",EDGE,"E102")}),1.0]])]});
            extrude(context, id + "F20", {"entities" : qUnion([Q0, Q1, Q2, Q3, Q4, Q5, Q6, Q7]), "depth" : 2.54 * mm});
        }
        {
            var Q0;
            Q0=makeQuery(id+"F20.opExtrude","CAP_EDGE",EDGE,{"disambiguationData":[OSD([sQuery(id+"F19.wireOp",EDGE,"E106")])],"isStart":false});
            var Q1;
            Q1=makeQuery(id+"F20.opExtrude","CAP_EDGE",EDGE,{"disambiguationData":[OSD([sQuery(id+"F19.wireOp",EDGE,"E102")])],"isStart":false});
            var Q2;
            Q2=makeQuery(id+"F20.opExtrude","CAP_EDGE",EDGE,{"disambiguationData":[OSD([sQuery(id+"F19.wireOp",EDGE,"E105")])],"isStart":false});
            var Q3;
            Q3=makeQuery(id+"F20.opExtrude","CAP_EDGE",EDGE,{"disambiguationData":[OSD([sQuery(id+"F19.wireOp",EDGE,"E107")])],"isStart":false});
            var Q4;
            Q4=makeQuery(id+"F20.opExtrude","CAP_EDGE",EDGE,{"disambiguationData":[OSD([sQuery(id+"F19.wireOp",EDGE,"E104")])],"isStart":false});
            var Q5;
            Q5=makeQuery(id+"F20.opExtrude","CAP_EDGE",EDGE,{"disambiguationData":[OSD([sQuery(id+"F19.wireOp",EDGE,"E108")])],"isStart":false});
            var Q6;
            Q6=makeQuery(id+"F20.opExtrude","CAP_EDGE",EDGE,{"disambiguationData":[OSD([sQuery(id+"F19.wireOp",EDGE,"E103")])],"isStart":false});
            fillet(context, id + "F21", {"entities" : qUnion([Q0, Q1, Q2, Q3, Q4, Q5, Q6]), "radius" : 2.54 * mm, "tangentPropagation" : true, "allowEdgeOverflow" : false});
        }
        {
            var Q0;
            Q0=qCreatedBy(makeId("Top.planeOp"),FACE);
            var sketch = newSketch(context, id + "F22", { "sketchPlane" : qUnion([Q0])});
            skCircle(sketch, "E109", {"center": v(46.89, 27.9) * mm, "radius": 8.18 * mm});
            skCircle(sketch, "E110", {"center": v(-48.54, -30.54) * mm, "radius": 8.25 * mm});
            skCircle(sketch, "E111", {"center": v(18.82, -17) * mm, "radius": 12.24 * mm});
            skSolve(sketch);
        }
        {
            var Q0;
            Q0=makeQuery(id+"F22.imprint","IMPRINT",FACE,{"disambiguationData":[TD([[makeQuery(id+"F22.imprint","IMPRINT",EDGE,{"derivedFrom":sQuery(id+"F22.wireOp",EDGE,"E110")}),1.0]])]});
            var Q1;
            Q1=makeQuery(id+"F22.imprint","IMPRINT",FACE,{"disambiguationData":[TD([[makeQuery(id+"F22.imprint","IMPRINT",EDGE,{"derivedFrom":sQuery(id+"F22.wireOp",EDGE,"E111")}),1.0]])]});
            var Q2;
            Q2=makeQuery(id+"F22.imprint","IMPRINT",FACE,{"disambiguationData":[TD([[makeQuery(id+"F22.imprint","IMPRINT",EDGE,{"derivedFrom":sQuery(id+"F22.wireOp",EDGE,"E109")}),1.0]])]});
            extrude(context, id + "F23", {"entities" : qUnion([Q0, Q1, Q2]), "depth" : 12.7 * mm});
        }
        {
            var Q0;
            Q0=makeQuery(id+"F23.opExtrude","CAP_EDGE",EDGE,{"disambiguationData":[OSD([sQuery(id+"F22.wireOp",EDGE,"E111")])],"isStart":false});
            var Q1;
            Q1=makeQuery(id+"F23.opExtrude","CAP_FACE",FACE,{"disambiguationData":[OSD([sQuery(id+"F22.wireOp",EDGE,"E109")])],"isStart":false});
            var Q2;
            Q2=makeQuery(id+"F23.opExtrude","CAP_EDGE",EDGE,{"disambiguationData":[OSD([sQuery(id+"F22.wireOp",EDGE,"E110")])],"isStart":false});
            fillet(context, id + "F24", {"entities" : qUnion([Q0, Q1, Q2]), "radius" : 7.62 * mm, "tangentPropagation" : true, "allowEdgeOverflow" : false});
        }
        {
            var Q0;
            Q0=qCreatedBy(makeId("Top.planeOp"),FACE);
            var sketch = newSketch(context, id + "F25", { "sketchPlane" : qUnion([Q0])});
            skCircle(sketch, "E112", {"center": v(31.03, 50.34) * mm, "radius": 2.58 * mm});
            skLineSegment(sketch, "E113", {"start": v(32.73, 52.28) * mm, "end": v(33.27, 52.7) * mm});
            skLineSegment(sketch, "E114", {"start": v(33.27, 52.7) * mm, "end": v(33.53, 52.51) * mm});
            skLineSegment(sketch, "E115", {"start": v(33.53, 52.51) * mm, "end": v(33.13, 51.83) * mm});
            skLineSegment(sketch, "E116", {"start": v(33.53, 49.7) * mm, "end": v(34.17, 49.37) * mm});
            skLineSegment(sketch, "E117", {"start": v(34.17, 49.37) * mm, "end": v(34, 49.06) * mm});
            skLineSegment(sketch, "E118", {"start": v(34, 49.06) * mm, "end": v(33.34, 49.2) * mm});
            skLineSegment(sketch, "E119", {"start": v(32.02, 47.95) * mm, "end": v(32.02, 47.4) * mm});
            skLineSegment(sketch, "E120", {"start": v(32.02, 47.4) * mm, "end": v(31.66, 47.4) * mm});
            skLineSegment(sketch, "E121", {"start": v(31.66, 47.4) * mm, "end": v(31.4, 47.78) * mm});
            skLineSegment(sketch, "E122", {"start": v(29.07, 48.66) * mm, "end": v(28.48, 48.43) * mm});
            skLineSegment(sketch, "E123", {"start": v(28.48, 48.43) * mm, "end": v(28.36, 48.74) * mm});
            skLineSegment(sketch, "E124", {"start": v(28.36, 48.74) * mm, "end": v(28.78, 49.06) * mm});
            skLineSegment(sketch, "E125", {"start": v(28.46, 50.64) * mm, "end": v(27.73, 50.92) * mm});
            skLineSegment(sketch, "E126", {"start": v(27.73, 50.92) * mm, "end": v(27.73, 51.3) * mm});
            skLineSegment(sketch, "E127", {"start": v(27.73, 51.3) * mm, "end": v(28.63, 51.3) * mm});
            skLineSegment(sketch, "E128", {"start": v(29.64, 52.51) * mm, "end": v(29.64, 53.17) * mm});
            skLineSegment(sketch, "E129", {"start": v(29.64, 53.17) * mm, "end": v(29.85, 53.33) * mm});
            skLineSegment(sketch, "E130", {"start": v(29.85, 53.33) * mm, "end": v(30.26, 52.8) * mm});
            skSolve(sketch);
        }
        {
            var Q0;
            Q0 = qSketchRegion(id + "F25", true);
            extrude(context, id + "F26", {"entities" : qUnion([Q0]), "depth" : 12.7 * mm});
        }
    });
